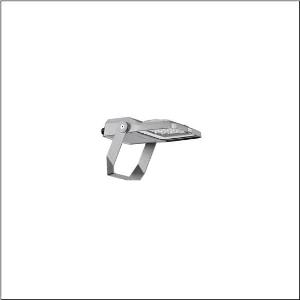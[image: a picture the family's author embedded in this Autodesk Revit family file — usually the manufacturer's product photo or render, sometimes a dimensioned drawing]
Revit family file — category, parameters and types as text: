
# Revit family: floodlight_fl_21_iq_micro___rs12_5xa7762a2b1a_2903
name_source: partatom
category: Lighting Fixtures
units: mm (PartAtom-declared; Revit-internal decimal feet)

## family parameters
Cut with Voids When Loaded = No
Host = Face
Light Source = No
Part Type = Normal
Room Calculation Point = No
Round Connector Dimension = Use Diameter
Shared = No

## types (1)
- --- (1 x LED, 3090 lm, 23.1 W, 3000K)
    Apparent Load = 23 VA
    CIE Flux Codes = 79 92 99 100 100
    Color Rendering = 70
    Color Temperature = 3000K
    Default Elevation = 1800 mm
    Description = Floodlight FL 21 iQ micro, floodlight, primary light control with lens, of PMMA, primary optical cover: protective disc, of toughened safety glass, transparent, light distribution: RS12, light emission: direct distribution, installation type: surface-mounted, LED, High Power LED, rated luminous flux: 3.090lm, luminous efficacy: 134lm/W, light colour: 730, colour temperature: 3000K, control: Auto-Match, Temp-Guard, Night-Set, Smart-Wire, Desk-Remote (wireless, voltage-free reading and setting of iQ features in the workshop via application-optimized NFC function/RFID function), optimised constant luminous flux control (CLO 2.0), Street-Remote, with terminal, 6-pole, mains connection: 220..240V, AC, 50/60Hz, start of lifetime: 23W, end of service life: 24W, reduction: 11W, luminaire housing, of diecast aluminium, powder-coated, Siteco® metallic grey (DB 702S), corrosivity category C5 mid according to DIN EN ISO 12944, sealing non-destructively replaceable, mounting bracket, of steel, galvanised, powder-coated, Siteco® metallic grey (DB 702S), protection rating (complete): IP66, insulation class (complete): insulation class II (safety insulation), certification: CE, ENEC, VDE, protection symbol: D, impact resistance: IK07, permissible operating ambient temperature: -40..+40°C, permissible operating ambient temperature for outdoor applications: -40..+50°C, standard: DIN EN 12944, LABS conformity tested according to VDMA 24364:2018-05, packaging unit: 1 piece

Light Distribution: RS12
    Height = 65 mm
    Lamp = 1 x LED
    Lamp Light Flux = 3090 lm
    Lamp Power = 23.1 W
    Lamp count = 1
    Length = 312 mm
    Luminous efficacy = 134 lm/W
    Manufacturer = Siteco
    ModVariant = No
    Model = 5XA7762A2B1A
    Number of Poles = 1
    OnlyDefault = Yes
    Power Factor = 1
    Product Name = Floodlight FL 21 iQ micro | RS12
    Product group = floodlight | pylon annexe
    ProductGroupID = 6200
    Protection Class = Protection class II
    Protection Degree = IP 66
    RLX_Detail_Level = 1
    RLX_Emergency_Light_Flux = 0 lm
    RLX_Emergency_Type = 0
    RLX_Emergency_Type_DB = No
    RlxData = <blob elided: 74893 chars, md5=96eb2617>
    Socket = socket
    Standby Power = 0 W
    System Light Flux = 3090 lm
    System Power = 23 W
    Type Comments = factory setting: luminous flux: 100 % | dim-lin: 254 | 455 mA
    Type Image = l_1006880.jpg
    URL = http://relux.com
    VarID = @adj_114937
    Voltage = 0 V
    Weight = 0.00 kg
    Width = 230 mm

## geometry (parser evidence)
native form markers: Blend x4, Sweep x12
no freeform markers — native parametric forms only
